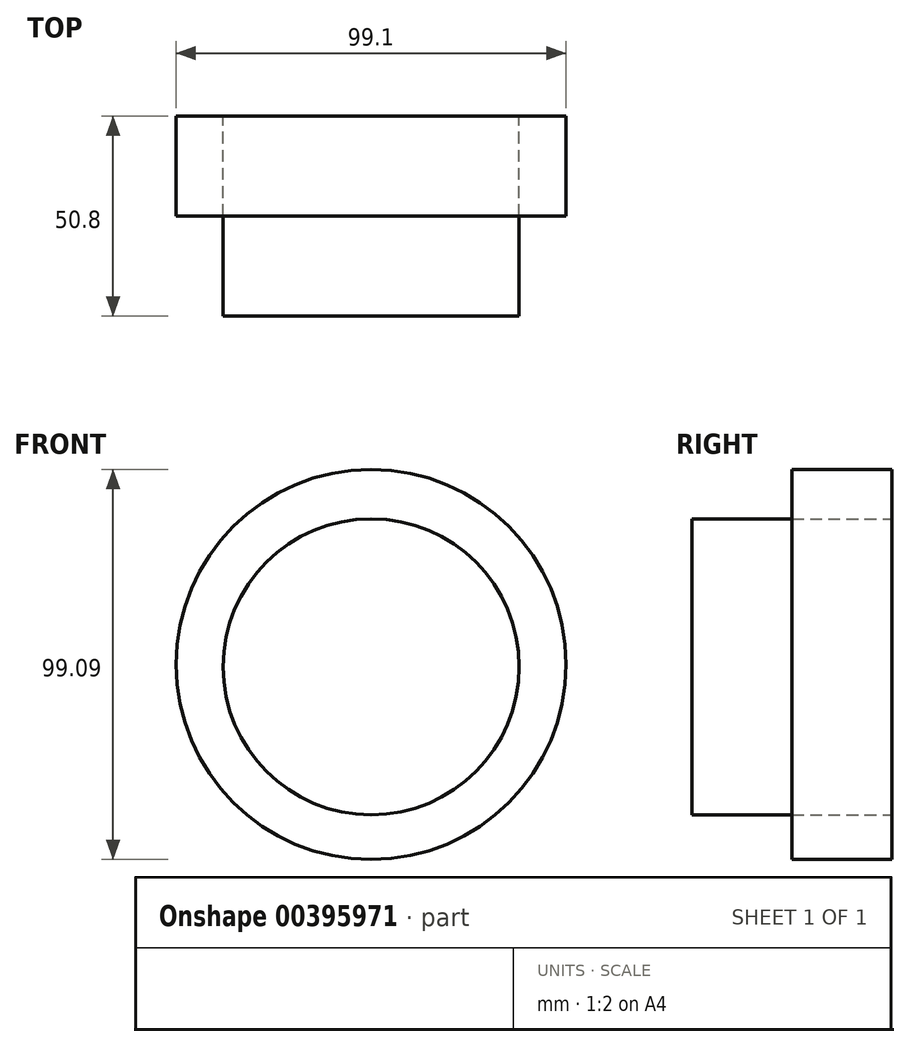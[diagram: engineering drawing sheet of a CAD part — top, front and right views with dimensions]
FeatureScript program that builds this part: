
annotation { "Feature Type Name" : "Feature", "Feature Type Description" : "" }
export const myFeature = defineFeature(function(context is Context, id is Id, definition is map)
    precondition{}
    {
        {
            var Q0;
            Q0=qCreatedBy(makeId("Front.planeOp"),FACE);
            var sketch = newSketch(context, id + "F0", { "sketchPlane" : qUnion([Q0])});
            skCircle(sketch, "E0", {"center": v(0, 22.94) * mm, "radius": 49.55 * mm});
            skSolve(sketch);
        }
        {
            var Q0;
            Q0=makeQuery(id+"F0.imprint","IMPRINT",FACE,{"disambiguationData":[TD([[makeQuery(id+"F0.imprint","IMPRINT",EDGE,{"derivedFrom":sQuery(id+"F0.wireOp",EDGE,"E0")}),1.0]])]});
            var sketch = newSketch(context, id + "F1", { "sketchPlane" : qUnion([Q0])});
            skCircle(sketch, "E1", {"center": v(0, 22.35) * mm, "radius": 37.62 * mm});
            skSolve(sketch);
        }
        {
            var Q0;
            Q0=makeQuery(id+"F0.imprint","IMPRINT",FACE,{"disambiguationData":[TD([[makeQuery(id+"F0.imprint","IMPRINT",EDGE,{"derivedFrom":sQuery(id+"F0.wireOp",EDGE,"E0")}),1.0]])]});
            var Q1;
            Q1=makeQuery(id+"F1.imprint","IMPRINT",FACE,{"disambiguationData":[TD([[makeQuery(id+"F1.imprint","IMPRINT",EDGE,{"derivedFrom":sQuery(id+"F1.wireOp",EDGE,"E1")}),1.0]])]});
            extrude(context, id + "F2", {"entities" : qUnion([Q0, Q1]), "depth" : 25.4 * mm});
        }
        {
            var Q0;
            Q0=makeQuery(id+"F2.opExtrude","CAP_FACE",FACE,{"disambiguationData":[OSD([sQuery(id+"F1.wireOp",EDGE,"E1")])],"isStart":false});
            extrude(context, id + "F3", {"entities" : qUnion([Q0]), "depth" : 25.4 * mm});
        }
    });
